FCSTD DOCUMENT  (FreeCAD 0.21R33668 +7 (Git))
Label: Headfixed Anaesthesia System
License: All rights reserved
LicenseURL: http://en.wikipedia.org/wiki/All_rights_reserved
objects: Sketcher::SketchObject×31, PartDesign::Pad×16, PartDesign::Pocket×10, Part::Feature×9, PartDesign::Body×5, Part::Box×2, Part::MultiCommon×2, Part::Mirroring×2, PartDesign::AdditiveLoft×2, PartDesign::LinearPattern×2, PartDesign::Chamfer×2, Mesh::Feature×1, Part::MultiFuse×1, Part::Cut×1, PartDesign::FeatureBase×1, Spreadsheet::Sheet×1, PartDesign::AdditivePipe×1, PartDesign::SubtractivePipe×1, PartDesign::Fillet×1, Part::Part2DObjectPython×1
note: 123 computed .brp shape members not serialized (recipe doc carries the construction recipe); baked Part::Feature solids carry a one-line shape summary decoded from their .brp

FEATURE [Mesh::Feature] MouseModel1_1_low_poly  label="MouseModel1.1_low_poly"
  Placement = pos=(-304.13,-78.83,-53.17) rot=(0,0,1;0rad)
FEATURE [Sketcher::SketchObject] Sketch  label="Mask profile"
  FullyConstrained = true
  MapMode = 5
  Placement = pos=(0,0,0) rot=(1,0,0;1.5708rad)
  Support = -> [XZ_Plane]
  expr: Constraints[19] = Spreadsheet.Hm
  expr: Constraints[20] = Spreadsheet.Wm
  expr: Constraints[21] = Spreadsheet.Rm
  expr: Constraints[27] = Spreadsheet.Ym
  sketch-geometry (12):
    g0: ArcOfCircle CenterX=-3.86 CenterY=1.095 CenterZ=0 NormalX=0 NormalY=0 NormalZ=1 AngleXU=0 Radius=2.26 StartAngle=1.5708 EndAngle=3.14159
    g1: LineSegment StartX=-3.86 StartY=3.355 StartZ=0 EndX=3.86 EndY=3.355 EndZ=0
    g2: ArcOfCircle CenterX=3.86 CenterY=1.095 CenterZ=0 NormalX=0 NormalY=0 NormalZ=1 AngleXU=0 Radius=2.26 StartAngle=1e-16 EndAngle=1.5708
    g3: LineSegment StartX=6.12 StartY=1.095 StartZ=0 EndX=6.12 EndY=-0.735 EndZ=0
    g4: ArcOfCircle CenterX=3.86 CenterY=-0.735 CenterZ=0 NormalX=0 NormalY=0 NormalZ=1 AngleXU=0 Radius=2.26 StartAngle=4.71239 EndAngle=6.28319
    g5: LineSegment StartX=3.86 StartY=-2.995 StartZ=0 EndX=-3.86 EndY=-2.995 EndZ=0
    g6: ArcOfCircle CenterX=-3.86 CenterY=-0.735 CenterZ=0 NormalX=0 NormalY=0 NormalZ=1 AngleXU=0 Radius=2.26 StartAngle=3.14159 EndAngle=4.71239
    g7: LineSegment StartX=-6.12 StartY=-0.735 StartZ=0 EndX=-6.12 EndY=1.095 EndZ=0
    g8: GeomPoint X=-6.12 Y=3.355 Z=0
    g9: GeomPoint X=6.12 Y=-2.995 Z=0
    g10: LineSegment StartX=-6.12 StartY=0.18 StartZ=0 EndX=6.12 EndY=0.18 EndZ=0
    g11: GeomPoint X=0 Y=0.18 Z=0
  constraints (28):
    c: Tangent(g0,g1) = 1.5708
    c: Tangent(g1,g2) = 1.5708
    c: Tangent(g2,g3) = 1.5708
    c: Tangent(g3,g4) = 1.5708
    c: Tangent(g4,g5) = 1.5708
    c: Tangent(g5,g6) = 1.5708
    c: Tangent(g6,g7) = 1.5708
    c: Tangent(g7,g0) = 1.5708
    c: Horizontal(g1)
    c: Horizontal(g5)
    c: Vertical(g3)
    c: Vertical(g7)
    c: Equal(g0,g2)
    c: Equal(g2,g4)
    c: PointOnObject(g8,g1)
    c: PointOnObject(g8,g7)
    c: PointOnObject(g9,g3)
    c: PointOnObject(g9,g5)
    c: Symmetric(g6,g4,g-2)
    c: DistanceY(g5,g0) = 6.35
    c: DistanceX(g0,g2) = 12.24
    c: Radius(g0) = 2.26
    c: PointOnObject(g10,g7)
    c: PointOnObject(g10,g3)
    c: Symmetric(g0,g5,g10)
    c: PointOnObject(g11,g10)
    c: PointOnObject(g11,g-2)
    c: DistanceY(g11) = 0.18
FEATURE [PartDesign::Pad] Pad
  Direction = (0,-1,-2e-16)
  Length = 1.5
  Length2 = 10
  Placement = pos=(0,0,0) rot=(1,0,0;1.5708rad)
  Profile = -> Sketch
  ReferenceAxis = -> Sketch [N_Axis]
  Type = 4
  expr: Length = Spreadsheet.YEm
FEATURE [PartDesign::Body] Body
  Group = -> [Sketch,Pad]
  Origin = -> Origin
  Tip = -> Pad
FEATURE [Part::Feature] MouseModel1_1_low_poly001_solid  label="MouseModel1_1_low_poly001 (Solid)"
  shape: large baked B-rep (84 MB .brp); summary skipped
FEATURE [Part::Feature] MouseModel1_1_low_poly001_solid001  label="MouseModel1_1_low_poly001 (Solid)001"
  shape: large baked B-rep (84 MB .brp); summary skipped
FEATURE [Part::Box] Box  label="Cube"
  AttacherType = Attacher::AttachEngine3D
  Height = 30
  Length = 40
  Placement = pos=(-20,-2,-12) rot=(0,0,1;0rad)
  Width = 30
FEATURE [Part::MultiCommon] Common
  Shapes = -> [MouseModel1_1_low_poly001_solid001,Box]
FEATURE [Part::Feature] Common001
  shape: bbox 33.9 x 28.08 x 25.21 mm, 16069 faces (baked)
FEATURE [Part::Box] Box001  label="Cube001"
  AttacherType = Attacher::AttachEngine3D
  Height = 20
  Length = 15
  Placement = pos=(-15,-1,-3.25) rot=(0,0,1;0rad)
  Width = 12
FEATURE [Part::MultiCommon] Common002
  Shapes = -> [Common001,Box001]
FEATURE [Part::Feature] Common002001
  shape: bbox 8.155 x 11.08 x 13.57 mm, 3527 faces (baked)
FEATURE [Part::Mirroring] Part__Mirroring  label="Common002001 (Mirror #1)"
  Base = (0,0,0)
  Normal = (1,0,0)
  Source = -> Common002001
FEATURE [Part::MultiFuse] Fusion
  Shapes = -> [Common002,Part__Mirroring]
FEATURE [Part::Cut] Cut
  Base = -> Body
  Tool = -> Fusion
FEATURE [PartDesign::FeatureBase] BaseFeature
  BaseFeature = -> Cut
FEATURE [Sketcher::SketchObject] Sketch002
  FullyConstrained = true
  MapMode = 5
  Placement = pos=(0,0,0) rot=(1,0,0;1.5708rad)
  Support = -> [XZ_Plane001]
  expr: Constraints[19] = Spreadsheet.Hm
  expr: Constraints[41] = Spreadsheet.Tm
  expr: Constraints[42] = Spreadsheet.Wm
  expr: Constraints[47] = Spreadsheet.Ym
  expr: Constraints[49] = Spreadsheet.Rm
  sketch-geometry (22):
    g0: ArcOfCircle CenterX=-3.86 CenterY=1.095 CenterZ=0 NormalX=0 NormalY=0 NormalZ=1 AngleXU=0 Radius=2.26 StartAngle=1.5708 EndAngle=3.14159
    g1: LineSegment StartX=-3.86 StartY=3.355 StartZ=0 EndX=3.86 EndY=3.355 EndZ=0
    g2: ArcOfCircle CenterX=3.86 CenterY=1.095 CenterZ=0 NormalX=0 NormalY=0 NormalZ=1 AngleXU=0 Radius=2.26 StartAngle=1e-16 EndAngle=1.5708
    g3: LineSegment StartX=6.12 StartY=1.095 StartZ=0 EndX=6.12 EndY=-0.735 EndZ=0
    g4: ArcOfCircle CenterX=3.86 CenterY=-0.735 CenterZ=0 NormalX=0 NormalY=0 NormalZ=1 AngleXU=0 Radius=2.26 StartAngle=4.71239 EndAngle=6.28319
    g5: LineSegment StartX=3.86 StartY=-2.995 StartZ=0 EndX=-3.86 EndY=-2.995 EndZ=0
    g6: ArcOfCircle CenterX=-3.86 CenterY=-0.735 CenterZ=0 NormalX=0 NormalY=0 NormalZ=1 AngleXU=0 Radius=2.26 StartAngle=3.14159 EndAngle=4.71239
    g7: LineSegment StartX=-6.12 StartY=-0.735 StartZ=0 EndX=-6.12 EndY=1.095 EndZ=0
    g8: GeomPoint X=-6.12 Y=3.355 Z=0
    g9: GeomPoint X=6.12 Y=-2.995 Z=0
    g10: ArcOfCircle CenterX=-3.86 CenterY=1.095 CenterZ=0 NormalX=0 NormalY=0 NormalZ=1 AngleXU=0 Radius=1.635 StartAngle=1.5708 EndAngle=3.14159
    g11: LineSegment StartX=-3.86 StartY=2.73 StartZ=0 EndX=3.86 EndY=2.73 EndZ=0
    g12: ArcOfCircle CenterX=3.86 CenterY=1.095 CenterZ=0 NormalX=0 NormalY=0 NormalZ=1 AngleXU=0 Radius=1.635 StartAngle=1e-16 EndAngle=1.5708
    g13: LineSegment StartX=5.495 StartY=1.095 StartZ=0 EndX=5.495 EndY=-0.735 EndZ=0
    g14: ArcOfCircle CenterX=3.86 CenterY=-0.735 CenterZ=0 NormalX=0 NormalY=0 NormalZ=1 AngleXU=0 Radius=1.635 StartAngle=4.71239 EndAngle=6.28319
    g15: LineSegment StartX=3.86 StartY=-2.37 StartZ=0 EndX=-3.86 EndY=-2.37 EndZ=0
    g16: ArcOfCircle CenterX=-3.86 CenterY=-0.735 CenterZ=0 NormalX=0 NormalY=0 NormalZ=1 AngleXU=0 Radius=1.635 StartAngle=3.14159 EndAngle=4.71239
    g17: LineSegment StartX=-5.495 StartY=-0.735 StartZ=0 EndX=-5.495 EndY=1.095 EndZ=0
    g18: GeomPoint X=-5.495 Y=2.73 Z=0
    g19: GeomPoint X=5.495 Y=-2.37 Z=0
    g20: LineSegment StartX=-6.12 StartY=0.18 StartZ=0 EndX=6.12 EndY=0.18 EndZ=0
    g21: GeomPoint X=0 Y=0.18 Z=0
  constraints (50):
    c: Tangent(g0,g1) = 1.5708
    c: Tangent(g1,g2) = 1.5708
    c: Tangent(g2,g3) = 1.5708
    c: Tangent(g3,g4) = 1.5708
    c: Tangent(g4,g5) = 1.5708
    c: Tangent(g5,g6) = 1.5708
    c: Tangent(g6,g7) = 1.5708
    c: Tangent(g7,g0) = 1.5708
    c: Horizontal(g1)
    c: Horizontal(g5)
    c: Vertical(g3)
    c: Vertical(g7)
    c: Equal(g0,g2)
    c: Equal(g2,g4)
    c: PointOnObject(g8,g1)
    c: PointOnObject(g8,g7)
    c: PointOnObject(g9,g3)
    c: PointOnObject(g9,g5)
    c: Symmetric(g6,g4,g-2)
    c: DistanceY(g5,g0) = 6.35
    c: Tangent(g10,g11) = 1.5708
    c: Tangent(g11,g12) = 1.5708
    c: Tangent(g12,g13) = 1.5708
    c: Tangent(g13,g14) = 1.5708
    c: Tangent(g14,g15) = 1.5708
    c: Tangent(g15,g16) = 1.5708
    c: Tangent(g16,g17) = 1.5708
    c: Tangent(g17,g10) = 1.5708
    c: Horizontal(g11)
    c: Horizontal(g15)
    c: Vertical(g13)
    c: Vertical(g17)
    c: Equal(g10,g12)
    c: Equal(g12,g14)
    c: Equal(g14,g16)
    c: PointOnObject(g18,g11)
    c: PointOnObject(g18,g17)
    c: PointOnObject(g19,g13)
    c: PointOnObject(g19,g15)
    c: Coincident(g0,g10)
    c: Coincident(g4,g14)
    c: DistanceX(g0,g10) = 0.625
    c: DistanceX(g0,g2) = 12.24
    c: PointOnObject(g20,g7)
    c: PointOnObject(g20,g3)
    c: PointOnObject(g21,g20)
    c: PointOnObject(g21,g-2)
    c: DistanceY(g21) = 0.18
    c: Symmetric(g0,g5,g20)
    c: Radius(g0) = 2.26
FEATURE [PartDesign::Pocket] Pocket
  BaseFeature = -> BaseFeature
  Direction = (0,1,2e-16)
  Length = 50
  Length2 = 0.875
  Profile = -> Sketch002
  ReferenceAxis = -> Sketch002 [N_Axis]
  Type = 4
  expr: Length2 = Spreadsheet.YEm - Spreadsheet.Tm
FEATURE [Spreadsheet::Sheet] Spreadsheet  label="params"
  cells = A4='Mask width; B4(Wm)==12.24 mm; A5='Mask height; B5(Hm)==6.35 mm; A6='Mask corner radius; B6(Rm)==2.26 mm; A7='Mask center y height; B7(Ym)==0.18 mm; A8='Mask thickness; B8(Tm)==0.625 mm; A9='Mask y extent; B9(YEm)==1.5 mm; A10='Tube outer diameter; B10(ODt)==0.125 "; A11='RightTubeZ; B11(Zrt)==Ym + Hm / 2 + ODt / 2 - Tm / 2 + 1 mm; A12='Tube inner diameter; B12(IDt)==3 " / 32; A13='Tube wall thickness; B13(WTt)==(ODt - IDt) / 2; A14='RightTubeY2; B14(Y2rt)==-YEm + Tm - WTt + ODt / 2 + ODt - WTt; A15='Mounting Hole X; B15(Xmh)==Xte + 12.75 mm - 25.5 mm - 2 mm; A16='Tube Y; B16(Yt)==YEm - Tm + WTt; A17='Mounting hole delta x; B17(DXmh)==0.25 "; A18='Mounting arm width; B18(Wma)==0.5 "; A19='Tube end X; B19(Xte)==30 mm
FEATURE [Sketcher::SketchObject] Sketch003  label="LeftTubeProfile"
  FullyConstrained = true
  MapMode = 5
  Placement = pos=(5.495,0,0) rot=(0.57735,-0.57735,-0.57735;2.0944rad)
  Support = -> [Pocket]
  expr: Constraints[1] = Spreadsheet.ODt
  expr: Constraints[4] = Spreadsheet.Yt
  sketch-geometry (2):
    g0: Circle CenterX=-0.315625 CenterY=0 CenterZ=0 NormalX=0 NormalY=0 NormalZ=1 AngleXU=0 Radius=1.5875
    g1: GeomPoint X=1.27188 Y=0 Z=0
  constraints (5):
    c: PointOnObject(g0,g-1)
    c: Diameter(g0) = 3.175
    c: PointOnObject(g1,g0)
    c: PointOnObject(g1,g-1)
    c: DistanceX(g1) = 1.27188
FEATURE [PartDesign::Pad] Pad001
  BaseFeature = -> Pocket
  Direction = (-1,0,0)
  Length = 24.5
  Length2 = 10
  Profile = -> Sketch003
  ReferenceAxis = -> Sketch003 [N_Axis]
  Reversed = true
  Type = 0
  expr: Length = Spreadsheet.Xte - 5.5 mm
FEATURE [Sketcher::SketchObject] Sketch004  label="RightTubeProfile"
  FullyConstrained = true
  MapMode = 5
  Placement = pos=(-5.495,0,0) rot=(0.57735,0.57735,0.57735;2.0944rad)
  Support = -> [Pad001]
  expr: Constraints[3] = -Spreadsheet.Yt
  expr: Constraints[4] = Spreadsheet.ODt
  sketch-geometry (2):
    g0: Circle CenterX=0.315625 CenterY=0 CenterZ=0 NormalX=0 NormalY=0 NormalZ=1 AngleXU=0 Radius=1.5875
    g1: GeomPoint X=-1.27188 Y=0 Z=0
  constraints (5):
    c: PointOnObject(g0,g-1)
    c: PointOnObject(g1,g0)
    c: PointOnObject(g1,g-1)
    c: DistanceX(g1) = -1.27188
    c: Diameter(g0) = 3.175
FEATURE [Sketcher::SketchObject] Sketch005  label="RightTubePath1"
  FullyConstrained = true
  MapMode = 5
  Placement = pos=(0,1.27188,0) rot=(1,0,0;1.5708rad)
  expr: .Placement.Base.y = Spreadsheet.Yt
  expr: Constraints[2] = -Spreadsheet.Wm / 2 + Spreadsheet.Tm
  expr: Constraints[3] = Spreadsheet.Tm
  expr: Constraints[6] = Spreadsheet.Zrt
  expr: Constraints[9] = Spreadsheet.Xte
  sketch-geometry (3):
    g0: LineSegment StartX=-5.495 StartY=0 StartZ=0 EndX=-6.12 EndY=4e-16 EndZ=0
    g1: ArcOfCircle CenterX=-6.12 CenterY=2.815 CenterZ=0 NormalX=0 NormalY=0 NormalZ=1 AngleXU=0 Radius=2.815 StartAngle=1.5708 EndAngle=4.71239
    g2: LineSegment StartX=-6.12 StartY=5.63 StartZ=0 EndX=30 EndY=5.63 EndZ=0
  constraints (10):
    c: PointOnObject(g0,g-1)
    c: PointOnObject(g0,g-1)
    c: DistanceX(g0) = -5.495
    c: DistanceX(g0,g0) = 0.625
    c: Tangent(g1,g0) = 1.5708
    c: DistanceX(g1,g1) = 0
    c: DistanceY(g1) = 5.63
    c: Coincident(g2,g1)
    c: Horizontal(g2)
    c: DistanceX(g2) = 30
FEATURE [PartDesign::AdditivePipe] AdditivePipe
  AuxilleryCurvelinear = true
  AuxillerySpineTangent = false
  BaseFeature = -> Pad001
  Binormal = (0,0,0)
  Mode = 0
  Profile = -> Sketch004
  Spine = -> Sketch005
  SpineTangent = false
  Transformation = 0
  Transition = 0
FEATURE [Sketcher::SketchObject] Sketch006  label="TubeJoiner"
  FullyConstrained = true
  MapMode = 5
  Placement = pos=(0,0.315625,0) rot=(1,0,0;1.5708rad)
  expr: .Placement.Base.y = -Spreadsheet.YEm + Spreadsheet.Tm - Spreadsheet.WTt + Spreadsheet.ODt / 2
  expr: Constraints[12] = Spreadsheet.Wm / 2 - Spreadsheet.Rm
  expr: Constraints[13] = Spreadsheet.Zrt
  expr: Constraints[28] = Spreadsheet.Xte - 7.5 mm - 0.9 mm
  expr: Constraints[8] = Spreadsheet.Ym + Spreadsheet.Hm / 2 - Spreadsheet.Rm
  expr: Constraints[9] = Spreadsheet.Rm
  sketch-geometry (9):
    g0: ArcOfCircle CenterX=3.86 CenterY=1.095 CenterZ=0 NormalX=0 NormalY=0 NormalZ=1 AngleXU=0 Radius=2.26 StartAngle=0 EndAngle=1.5708
    g1: LineSegment StartX=6.12 StartY=1.095 StartZ=0 EndX=6.12 EndY=0 EndZ=0
    g2: LineSegment StartX=6.12 StartY=0 StartZ=0 EndX=21.6 EndY=0 EndZ=0
    g3: LineSegment StartX=21.6 StartY=0 StartZ=0 EndX=21.6 EndY=5.63 EndZ=0
    g4: LineSegment StartX=21.6 StartY=5.63 StartZ=0 EndX=-6.12 EndY=5.63 EndZ=0
    g5: ArcOfCircle CenterX=-6.12 CenterY=2.815 CenterZ=0 NormalX=0 NormalY=0 NormalZ=1 AngleXU=0 Radius=2.815 StartAngle=1.5708 EndAngle=4.71239
    g6: ArcOfCircle CenterX=-3.86 CenterY=1.095 CenterZ=0 NormalX=0 NormalY=0 NormalZ=1 AngleXU=0 Radius=2.26 StartAngle=1.5708 EndAngle=3.14159
    g7: LineSegment StartX=-6.12 StartY=1.095 StartZ=0 EndX=-6.12 EndY=0 EndZ=0
    g8: LineSegment StartX=-3.86 StartY=3.355 StartZ=0 EndX=3.86 EndY=3.355 EndZ=0
  constraints (29):
    c: Coincident(g1,g0)
    c: Vertical(g1)
    c: Coincident(g1,g2)
    c: Horizontal(g2)
    c: Coincident(g2,g3)
    c: Vertical(g3)
    c: Coincident(g3,g4)
    c: Horizontal(g4)
    c: DistanceY(g0) = 1.095
    c: Radius(g0) = 2.26
    c: DistanceX(g0,g0) = 0
    c: DistanceY(g0,g0) = 0
    c: DistanceX(g0) = 3.86
    c: DistanceY(g4) = 5.63
    c: DistanceY(g2) = 0
    c: Coincident(g5,g4)
    c: PointOnObject(g5,g-1)
    c: Coincident(g7,g6)
    c: Coincident(g7,g5)
    c: Coincident(g8,g6)
    c: Coincident(g8,g0)
    c: Horizontal(g8)
    c: DistanceY(g6,g6) = 0
    c: DistanceX(g6,g6) = 0
    c: Vertical(g7)
    c: DistanceX(g5,g5) = 0
    c: DistanceX(g5,g4) = 0
    c: Symmetric(g6,g0,g-2)
    c: DistanceX(g3) = 21.6
FEATURE [PartDesign::Pad] Pad002
  BaseFeature = -> AdditivePipe
  Direction = (0,-1,2e-16)
  Length = 3.175
  Length2 = 10
  Midplane = true
  Profile = -> Sketch006
  ReferenceAxis = -> Sketch006 [N_Axis]
  Type = 0
  expr: Length = Spreadsheet.ODt
FEATURE [Sketcher::SketchObject] Sketch007  label="LeftTubeProfile001"
  FullyConstrained = true
  MapMode = 5
  Placement = pos=(5.495,0,0) rot=(0.57735,-0.57735,-0.57735;2.0944rad)
  Support = -> [Pocket]
  expr: Constraints[1] = Spreadsheet.ODt
  expr: Constraints[4] = Spreadsheet.YEm - Spreadsheet.Tm + Spreadsheet.WTt
  expr: Constraints[6] = Spreadsheet.IDt
  sketch-geometry (3):
    g0: Circle CenterX=-0.315625 CenterY=0 CenterZ=0 NormalX=0 NormalY=0 NormalZ=1 AngleXU=0 Radius=1.5875
    g1: GeomPoint X=1.27188 Y=0 Z=0
    g2: Circle CenterX=-0.315625 CenterY=0 CenterZ=0 NormalX=0 NormalY=0 NormalZ=1 AngleXU=0 Radius=1.19062
  constraints (7):
    c: PointOnObject(g0,g-1)
    c: Diameter(g0) = 3.175
    c: PointOnObject(g1,g0)
    c: PointOnObject(g1,g-1)
    c: DistanceX(g1) = 1.27188
    c: Coincident(g2,g0)
    c: Diameter(g2) = 2.38125
FEATURE [Sketcher::SketchObject] Sketch008  label="RightTubeProfile001"
  FullyConstrained = true
  MapMode = 5
  Placement = pos=(-5.495,0,0) rot=(0.57735,0.57735,0.57735;2.0944rad)
  Support = -> [Pad001]
  expr: Constraints[3] = -Spreadsheet.YEm + Spreadsheet.Tm - Spreadsheet.WTt
  expr: Constraints[4] = Spreadsheet.ODt
  expr: Constraints[6] = Spreadsheet.IDt
  sketch-geometry (3):
    g0: Circle CenterX=0.315625 CenterY=0 CenterZ=0 NormalX=0 NormalY=0 NormalZ=1 AngleXU=0 Radius=1.5875
    g1: GeomPoint X=-1.27188 Y=0 Z=0
    g2: Circle CenterX=0.315625 CenterY=0 CenterZ=0 NormalX=0 NormalY=0 NormalZ=1 AngleXU=0 Radius=1.19062
  constraints (7):
    c: PointOnObject(g0,g-1)
    c: PointOnObject(g1,g0)
    c: PointOnObject(g1,g-1)
    c: DistanceX(g1) = -1.27188
    c: Diameter(g0) = 3.175
    c: Coincident(g2,g0)
    c: Diameter(g2) = 2.38125
FEATURE [PartDesign::Pocket] Pocket001
  BaseFeature = -> Pad002
  Direction = (1,0,0)
  Length = 5
  Length2 = 5
  Profile = -> Sketch007
  ReferenceAxis = -> Sketch007 [N_Axis]
  Type = 1
FEATURE [PartDesign::SubtractivePipe] SubtractivePipe
  AuxilleryCurvelinear = true
  AuxillerySpineTangent = false
  BaseFeature = -> Pocket001
  Binormal = (0,0,0)
  Mode = 0
  Profile = -> Sketch008
  Spine = -> Sketch005
  SpineTangent = false
  Transformation = 0
  Transition = 0
FEATURE [Part::Feature] Part__Feature  label="5372K511_Plastic Barbed Tube Fitting for Air and Water"
  Placement = pos=(30.46,-4.33,0) rot=(0,0,1;0rad)
  shape: bbox 22.86 x 4.562 x 4.562 mm, 34 faces (baked)
FEATURE [Sketcher::SketchObject] Sketch009  label="BarbProfile1"
  FullyConstrained = true
  MapMode = 5
  Placement = pos=(30,0,0) rot=(0.57735,0.57735,0.57735;2.0944rad)
  Support = -> [SubtractivePipe]
  expr: Constraints[1] = Spreadsheet.IDt
  expr: Constraints[2] = Spreadsheet.ODt
  expr: Constraints[3] = Spreadsheet.Zrt
  expr: Constraints[4] = -Spreadsheet.YEm + Spreadsheet.Tm - Spreadsheet.WTt + Spreadsheet.ODt / 2
  sketch-geometry (2):
    g0: Circle CenterX=0.315625 CenterY=5.63 CenterZ=0 NormalX=0 NormalY=0 NormalZ=1 AngleXU=0 Radius=1.5875
    g1: Circle CenterX=0.315625 CenterY=5.63 CenterZ=0 NormalX=0 NormalY=0 NormalZ=1 AngleXU=0 Radius=1.19062
  constraints (5):
    c: Coincident(g1,g0)
    c: Diameter(g1) = 2.38125
    c: Diameter(g0) = 3.175
    c: DistanceY(g0) = 5.63
    c: DistanceX(g0) = 0.315625
FEATURE [Sketcher::SketchObject] Sketch010  label="BarbProfile2"
  FullyConstrained = true
  MapMode = 5
  Placement = pos=(28.1,0,0) rot=(0.57735,0.57735,0.57735;2.0944rad)
  expr: .Placement.Base.x = Spreadsheet.Xte - 1.9 mm
  expr: Constraints[1] = Spreadsheet.IDt
  expr: Constraints[2] = Spreadsheet.ODt + 0.31 mm
  expr: Constraints[3] = Spreadsheet.Zrt
  expr: Constraints[4] = -Spreadsheet.YEm + Spreadsheet.Tm - Spreadsheet.WTt + Spreadsheet.ODt / 2
  sketch-geometry (2):
    g0: Circle CenterX=0.315625 CenterY=5.63 CenterZ=0 NormalX=0 NormalY=0 NormalZ=1 AngleXU=0 Radius=1.7425
    g1: Circle CenterX=0.315625 CenterY=5.63 CenterZ=0 NormalX=0 NormalY=0 NormalZ=1 AngleXU=0 Radius=1.19062
  constraints (5):
    c: Coincident(g1,g0)
    c: Diameter(g1) = 2.38125
    c: Diameter(g0) = 3.485
    c: DistanceY(g0) = 5.63
    c: DistanceX(g0) = 0.315625
FEATURE [PartDesign::AdditiveLoft] AdditiveLoft
  BaseFeature = -> SubtractivePipe
  Closed = false
  Profile = -> Sketch009
  Ruled = false
  Sections = -> [Sketch010]
FEATURE [PartDesign::LinearPattern] LinearPattern
  BaseFeature = -> AdditiveLoft
  Direction = -> Sketch009 [N_Axis]
  Length = 3.8
  Occurrences = 3
  Originals = -> [AdditiveLoft]
  Reversed = true
  expr: Length = 1.9 mm * 2
FEATURE [Sketcher::SketchObject] Sketch011  label="BarbProfile003"
  FullyConstrained = true
  MapMode = 5
  Placement = pos=(30,0,0) rot=(0.57735,0.57735,0.57735;2.0944rad)
  Support = -> [SubtractivePipe]
  expr: Constraints[1] = Spreadsheet.IDt
  expr: Constraints[2] = Spreadsheet.ODt
  expr: Constraints[3] = -Spreadsheet.YEm + Spreadsheet.Tm - Spreadsheet.WTt + Spreadsheet.ODt / 2
  sketch-geometry (2):
    g0: Circle CenterX=0.315625 CenterY=0 CenterZ=0 NormalX=0 NormalY=0 NormalZ=1 AngleXU=0 Radius=1.5875
    g1: Circle CenterX=0.315625 CenterY=0 CenterZ=0 NormalX=0 NormalY=0 NormalZ=1 AngleXU=0 Radius=1.19062
  constraints (5):
    c: Coincident(g1,g0)
    c: Diameter(g1) = 2.38125
    c: Diameter(g0) = 3.175
    c: DistanceX(g0) = 0.315625
    c: DistanceY(g0) = 0
FEATURE [Sketcher::SketchObject] Sketch012  label="BarbProfile004"
  FullyConstrained = true
  MapMode = 5
  Placement = pos=(28.1,0,0) rot=(0.57735,0.57735,0.57735;2.0944rad)
  expr: .Placement.Base.x = Spreadsheet.Xte - 1.9 mm
  expr: Constraints[1] = Spreadsheet.IDt
  expr: Constraints[2] = Spreadsheet.ODt + 0.31 mm
  expr: Constraints[4] = -Spreadsheet.YEm + Spreadsheet.Tm - Spreadsheet.WTt + Spreadsheet.ODt / 2
  sketch-geometry (2):
    g0: Circle CenterX=0.315625 CenterY=0 CenterZ=0 NormalX=0 NormalY=0 NormalZ=1 AngleXU=0 Radius=1.7425
    g1: Circle CenterX=0.315625 CenterY=0 CenterZ=0 NormalX=0 NormalY=0 NormalZ=1 AngleXU=0 Radius=1.19062
  constraints (5):
    c: Coincident(g1,g0)
    c: Diameter(g1) = 2.38125
    c: Diameter(g0) = 3.485
    c: DistanceY(g0) = 0
    c: DistanceX(g0) = 0.315625
FEATURE [PartDesign::AdditiveLoft] AdditiveLoft001
  BaseFeature = -> LinearPattern
  Closed = false
  Profile = -> Sketch011
  Ruled = false
  Sections = -> [Sketch012]
FEATURE [PartDesign::LinearPattern] LinearPattern001
  BaseFeature = -> AdditiveLoft001
  Direction = -> Sketch011 [N_Axis]
  Length = 3.8
  Occurrences = 3
  Originals = -> [AdditiveLoft001]
  Reversed = true
  expr: Length = 1.9 mm * 2
FEATURE [Sketcher::SketchObject] Sketch013  label="Mounting holes"
  FullyConstrained = true
  MapMode = 5
  Placement = pos=(0,-1.27187,3e-16) rot=(1,0,0;1.5708rad)
  Support = -> [LinearPattern001]
  expr: Constraints[0] = 0.12 "
  expr: Constraints[15] = Spreadsheet.Xmh
  expr: Constraints[16] = Spreadsheet.DXmh
  expr: Constraints[1] = Spreadsheet.Zrt / 2
  expr: Constraints[5] = 0.219 "
  sketch-geometry (8):
    g0: Circle CenterX=12.075 CenterY=2.815 CenterZ=0 NormalX=0 NormalY=0 NormalZ=1 AngleXU=0 Radius=1.524
    g1: Circle CenterX=18.425 CenterY=2.815 CenterZ=0 NormalX=0 NormalY=0 NormalZ=1 AngleXU=0 Radius=1.524
    g2: Circle CenterX=12.075 CenterY=2.815 CenterZ=0 NormalX=0 NormalY=0 NormalZ=1 AngleXU=0 Radius=2.84073
    g3: Circle CenterX=18.425 CenterY=2.815 CenterZ=0 NormalX=0 NormalY=0 NormalZ=1 AngleXU=0 Radius=2.84073
    g4: GeomPoint X=15.5843 Y=2.815 Z=0
    g5: GeomPoint X=14.9157 Y=2.815 Z=0
    g6: LineSegment StartX=12.075 StartY=2.815 StartZ=0 EndX=18.425 EndY=2.815 EndZ=0
    g7: GeomPoint X=15.25 Y=2.815 Z=0
  constraints (17):
    c: Diameter(g0) = 3.048
    c: DistanceY(g0) = 2.815
    c: Equal(g1,g0)
    c: DistanceY(g0,g1) = 0
    c: Coincident(g2,g0)
    c: Diameter(g2) = 5.68146
    c: Coincident(g3,g1)
    c: Equal(g3,g2)
    c: PointOnObject(g4,g3)
    c: PointOnObject(g5,g2)
    c: Coincident(g6,g0)
    c: Coincident(g6,g1)
    c: PointOnObject(g4,g6)
    c: PointOnObject(g5,g6)
    c: Symmetric(g0,g1,g7)
    c: DistanceX(g7) = 15.25
    c: DistanceX(g0,g1) = 6.35
FEATURE [PartDesign::Pocket] Pocket002
  BaseFeature = -> LinearPattern001
  Direction = (0,1,-2e-16)
  Length = 5
  Length2 = 5
  Profile = -> Sketch013
  ReferenceAxis = -> Sketch013 [N_Axis]
  Type = 1
FEATURE [PartDesign::Body] Body001  label="Mask"
  BaseFeature = -> Cut
  Group = -> [BaseFeature,Sketch002,Pocket,Sketch003,Pad001,Sketch004,Sketch005,AdditivePipe,Sketch006,Pad002,Sketch007,Sketch008,Pocket001,SubtractivePipe,Sketch009,Sketch010,AdditiveLoft,LinearPattern,Sketch011,Sketch012,AdditiveLoft001,LinearPattern001,Sketch013,Pocket002]
  Origin = -> Origin001
  Tip = -> Pocket002
FEATURE [Sketcher::SketchObject] Sketch014  label="ConnectorProfile"
  FullyConstrained = true
  MapMode = 5
  Placement = pos=(15.25,0,0) rot=(0.57735,0.57735,0.57735;2.0944rad)
  expr: .Placement.Base.x = Spreadsheet.Xmh
  expr: Constraints[23] = -Spreadsheet.Yt
  expr: Constraints[24] = Spreadsheet.ODt
  expr: Constraints[25] = 1.1 * Spreadsheet.ODt
  expr: Constraints[27] = Spreadsheet.Zrt
  expr: Constraints[28] = Spreadsheet.ODt * 2
  sketch-geometry (12):
    g0: ArcOfCircle CenterX=0.315625 CenterY=0 CenterZ=0 NormalX=0 NormalY=0 NormalZ=1 AngleXU=0 Radius=1.74625 StartAngle=3.14159 EndAngle=6.28319
    g1: ArcOfCircle CenterX=0.315625 CenterY=0 CenterZ=0 NormalX=0 NormalY=0 NormalZ=1 AngleXU=0 Radius=3.175 StartAngle=4.71239 EndAngle=6.28319
    g2: ArcOfCircle CenterX=-1.43063 CenterY=4.20125 CenterZ=0 NormalX=0 NormalY=0 NormalZ=1 AngleXU=0 Radius=1.42875 StartAngle=1.5708 EndAngle=3.14159
    g3: ArcOfCircle CenterX=2.06188 CenterY=4.20125 CenterZ=0 NormalX=0 NormalY=0 NormalZ=1 AngleXU=0 Radius=1.42875 StartAngle=0 EndAngle=1.5708
    g4: LineSegment StartX=-2.85937 StartY=4.20125 StartZ=0 EndX=-2.85937 EndY=-3.175 EndZ=0
    g5: LineSegment StartX=-1.43063 StartY=5.63 StartZ=0 EndX=-1.43063 EndY=0 EndZ=0
    g6: LineSegment StartX=2.06188 StartY=5.63 StartZ=0 EndX=2.06188 EndY=0 EndZ=0
    g7: LineSegment StartX=3.49062 StartY=4.20125 StartZ=0 EndX=3.49062 EndY=-9e-16 EndZ=0
    g8: Circle CenterX=0.315625 CenterY=0 CenterZ=0 NormalX=0 NormalY=0 NormalZ=1 AngleXU=0 Radius=1.5875
    g9: GeomPoint X=-1.27188 Y=0 Z=0
    g10: LineSegment StartX=-2.85937 StartY=-3.175 StartZ=0 EndX=0.315625 EndY=-3.175 EndZ=0
    g11: LineSegment StartX=0.315625 StartY=0 StartZ=0 EndX=0.315625 EndY=-3.175 EndZ=0
  constraints (35):
    c: PointOnObject(g0,g-1)
    c: PointOnObject(g0,g-1)
    c: PointOnObject(g0,g-1)
    c: Coincident(g1,g0)
    c: PointOnObject(g1,g-1)
    c: Coincident(g4,g2)
    c: Vertical(g4)
    c: Coincident(g5,g2)
    c: Coincident(g5,g0)
    c: Coincident(g6,g3)
    c: Coincident(g6,g0)
    c: Coincident(g7,g3)
    c: Coincident(g7,g1)
    c: Vertical(g7)
    c: Vertical(g5)
    c: Vertical(g6)
    c: Equal(g3,g2)
    c: PointOnObject(g2,g5)
    c: DistanceY(g2,g2) = 0
    c: DistanceY(g3,g3) = 0
    c: Coincident(g8,g0)
    c: PointOnObject(g9,g8)
    c: PointOnObject(g9,g-1)
    c: DistanceX(g9) = -1.27188
    c: Diameter(g8) = 3.175
    c: Diameter(g0) = 3.4925
    c: DistanceY(g3,g2) = 0
    c: DistanceY(g2) = 5.63
    c: Diameter(g1) = 6.35
    c: Coincident(g10,g4)
    c: Coincident(g10,g1)
    c: Horizontal(g10)
    c: Coincident(g11,g0)
    c: Coincident(g1,g11)
    c: Symmetric(g2,g3,g11)
FEATURE [PartDesign::Pad] Pad003
  Direction = (1,0,0)
  Length = 12.7
  Length2 = 10
  Midplane = true
  Placement = pos=(15.25,0,0) rot=(0.57735,0.57735,0.57735;2.0944rad)
  Profile = -> Sketch014
  ReferenceAxis = -> Sketch014 [N_Axis]
  Type = 0
  expr: Length = Spreadsheet.Wma
FEATURE [Sketcher::SketchObject] Sketch015  label="Mounting holes001"
  FullyConstrained = true
  MapMode = 5
  Placement = pos=(0,-1.27187,3e-16) rot=(1,0,0;1.5708rad)
  Support = -> [LinearPattern001]
  expr: Constraints[0] = 0.12 "
  expr: Constraints[15] = Spreadsheet.Xmh
  expr: Constraints[16] = Spreadsheet.DXmh
  expr: Constraints[1] = Spreadsheet.Zrt / 2
  expr: Constraints[5] = 0.219 "
  sketch-geometry (8):
    g0: Circle CenterX=12.075 CenterY=2.815 CenterZ=0 NormalX=0 NormalY=0 NormalZ=1 AngleXU=0 Radius=1.524
    g1: Circle CenterX=18.425 CenterY=2.815 CenterZ=0 NormalX=0 NormalY=0 NormalZ=1 AngleXU=0 Radius=1.524
    g2: Circle CenterX=12.075 CenterY=2.815 CenterZ=0 NormalX=0 NormalY=0 NormalZ=1 AngleXU=0 Radius=2.84073
    g3: Circle CenterX=18.425 CenterY=2.815 CenterZ=0 NormalX=0 NormalY=0 NormalZ=1 AngleXU=0 Radius=2.84073
    g4: GeomPoint X=15.5843 Y=2.815 Z=0
    g5: GeomPoint X=14.9157 Y=2.815 Z=0
    g6: LineSegment StartX=12.075 StartY=2.815 StartZ=0 EndX=18.425 EndY=2.815 EndZ=0
    g7: GeomPoint X=15.25 Y=2.815 Z=0
  constraints (17):
    c: Diameter(g0) = 3.048
    c: DistanceY(g0) = 2.815
    c: Equal(g1,g0)
    c: DistanceY(g0,g1) = 0
    c: Coincident(g2,g0)
    c: Diameter(g2) = 5.68146
    c: Coincident(g3,g1)
    c: Equal(g3,g2)
    c: PointOnObject(g4,g3)
    c: PointOnObject(g5,g2)
    c: Coincident(g6,g0)
    c: Coincident(g6,g1)
    c: PointOnObject(g4,g6)
    c: PointOnObject(g5,g6)
    c: Symmetric(g0,g1,g7)
    c: DistanceX(g7) = 15.25
    c: DistanceX(g0,g1) = 6.35
FEATURE [PartDesign::Pocket] Pocket003
  BaseFeature = -> Pad003
  Direction = (0,1,-2e-16)
  Length = 5
  Length2 = 5
  Midplane = true
  Placement = pos=(15.25,0,0) rot=(0.57735,0.57735,0.57735;2.0944rad)
  Profile = -> Sketch015
  ReferenceAxis = -> Sketch015 [N_Axis]
  Type = 1
FEATURE [Sketcher::SketchObject] Sketch016  label="Mounting arm profile"
  FullyConstrained = true
  MapMode = 5
  Placement = pos=(15.25,-2.85937,2e-16) rot=(0.57735,0.57735,-0.57735;2.0944rad)
  Support = -> [Pocket003]
  expr: Constraints[13] = Spreadsheet.DXmh
  expr: Constraints[14] = -Spreadsheet.Zrt / 2
  expr: Constraints[15] = 0.219 "
  expr: Constraints[16] = Spreadsheet.Wma
  expr: Constraints[18] = Spreadsheet.ODt
  sketch-geometry (8):
    g0: LineSegment StartX=3.175 StartY=6.35 StartZ=0 EndX=0 EndY=6.35 EndZ=0
    g1: LineSegment StartX=0 StartY=6.35 StartZ=0 EndX=0 EndY=-6.35 EndZ=0
    g2: LineSegment StartX=0 StartY=-6.35 StartZ=0 EndX=3.175 EndY=-6.35 EndZ=0
    g3: LineSegment StartX=3.175 StartY=-6.35 StartZ=0 EndX=3.175 EndY=6.35 EndZ=0
    g4: Circle CenterX=-2.815 CenterY=3.175 CenterZ=0 NormalX=0 NormalY=0 NormalZ=1 AngleXU=0 Radius=2.7813
    g5: Circle CenterX=-2.815 CenterY=-3.175 CenterZ=0 NormalX=0 NormalY=0 NormalZ=1 AngleXU=0 Radius=2.7813
    g6: GeomPoint X=-2.815 Y=0.3937 Z=0
    g7: GeomPoint X=-2.815 Y=-0.3937 Z=0
  constraints (20):
    c: Coincident(g0,g1)
    c: Coincident(g1,g2)
    c: Coincident(g2,g3)
    c: Coincident(g3,g0)
    c: Horizontal(g0)
    c: Horizontal(g2)
    c: Vertical(g1)
    c: Equal(g5,g4)
    c: Symmetric(g5,g4,g-1)
    c: PointOnObject(g6,g4)
    c: PointOnObject(g7,g5)
    c: DistanceX(g6,g4) = 0
    c: DistanceX(g7,g5) = 0
    c: DistanceY(g5,g4) = 6.35
    c: DistanceX(g4) = -2.815
    c: Diameter(g4) = 5.5626
    c: DistanceY(g3,g3) = 12.7
    c: Symmetric(g0,g2,g-1)
    c: DistanceX(g0) = 3.175
    c: DistanceX(g0,g0) = 3.175
FEATURE [Sketcher::SketchObject] Sketch020  label="Mounting platform"
  FullyConstrained = false
  MapMode = 5
  Support = -> [XY_Plane003]
  sketch-geometry (4):
    g0: LineSegment StartX=-25.4 StartY=3.175 StartZ=0 EndX=0 EndY=3.175 EndZ=0
    g1: LineSegment StartX=0 StartY=3.175 StartZ=0 EndX=0 EndY=0 EndZ=0
    g2: LineSegment StartX=0 StartY=0 StartZ=0 EndX=-25.4 EndY=0 EndZ=0
    g3: LineSegment StartX=-25.4 StartY=0 StartZ=0 EndX=-25.4 EndY=3.175 EndZ=0
  constraints (11):
    c: Coincident(g0,g1)
    c: Coincident(g1,g2)
    c: Coincident(g2,g3)
    c: Coincident(g3,g0)
    c: Horizontal(g0)
    c: Horizontal(g2)
    c: Vertical(g1)
    c: Vertical(g3)
    c: DistanceX(g2,g2) = 25.4
    c: DistanceY(g1,g1) = 3.175
    c: Coincident(g-1,g1)
FEATURE [PartDesign::Pad] Pad005
  AllowMultiFace = false
  Direction = (1,1,1)
  Length = 25.4
  Length2 = 99.9998
  Profile = -> Sketch020
  Type = 0
FEATURE [Sketcher::SketchObject] Sketch001  label="Spout support platform"
  FullyConstrained = false
  MapMode = 5
  Placement = pos=(0,3.175,0) rot=(0,0.707107,0.707107;3.14159rad)
  Support = -> [Pad005]
  expr: Constraints[11] = 1.5 in - 0.375 in
  expr: Constraints[8] = (1 in - 0.4 in) / 2
  sketch-geometry (4):
    g0: LineSegment StartX=-28.575 StartY=17.78 StartZ=0 EndX=0 EndY=17.78 EndZ=0
    g1: LineSegment StartX=0 StartY=17.78 StartZ=0 EndX=0 EndY=7.62 EndZ=0
    g2: LineSegment StartX=0 StartY=7.62 StartZ=0 EndX=-28.575 EndY=7.62 EndZ=0
    g3: LineSegment StartX=-28.575 StartY=7.62 StartZ=0 EndX=-28.575 EndY=17.78 EndZ=0
  constraints (12):
    c: Coincident(g0,g1)
    c: Coincident(g1,g2)
    c: Coincident(g2,g3)
    c: Coincident(g3,g0)
    c: Horizontal(g0)
    c: Horizontal(g2)
    c: Vertical(g1)
    c: Vertical(g3)
    c: DistanceY(g-1,g1) = 7.62
    c: DistanceY(g1,g1) = 10.16
    c: DistanceX(g1,g-1) = 0
    c: DistanceX(g2,g2) = 28.575
FEATURE [PartDesign::Pad] Pad006
  AllowMultiFace = false
  BaseFeature = -> Pad005
  Direction = (1,1,1)
  Length = 1.81
  Length2 = 4.445
  Profile = -> Sketch001
  Type = 4
  expr: Length = 1.81 mm
FEATURE [Sketcher::SketchObject] Sketch021  label="Spout groove"
  FullyConstrained = false
  MapMode = 5
  Placement = pos=(28.575,0,0) rot=(0.57735,0.57735,0.57735;2.0944rad)
  Support = -> [Pad006]
  expr: Constraints[3] = 1.81 mm / 2
  expr: Constraints[7] = 0.125 " + 1.81 mm / 2
  sketch-geometry (4):
    g0: LineSegment StartX=9.15014 StartY=19.05 StartZ=0 EndX=2.80014 EndY=12.7 EndZ=0
    g1: LineSegment StartX=2.80014 StartY=12.7 StartZ=0 EndX=9.15014 EndY=6.35 EndZ=0
    g2: LineSegment StartX=9.15014 StartY=6.35 StartZ=0 EndX=9.15014 EndY=19.05 EndZ=0
    g3: Circle CenterX=4.08 CenterY=12.7 CenterZ=0 NormalX=0 NormalY=0 NormalZ=1 AngleXU=0 Radius=0.905
  constraints (12):
    c: Coincident(g0,g2)
    c: Coincident(g0,g1)
    c: Coincident(g1,g2)
    c: Radius(g3) = 0.905
    c: Tangent(g1,g3)
    c: Tangent(g3,g0)
    c: DistanceX(g1,g0) = 0
    c: DistanceX(g-1,g3) = 4.08
    c: DistanceY(g-1,g0) = 12.7
    c: Equal(g0,g1)
    c: Angle(g1,g0) = 1.5708
    c: DistanceX(g0,g1) = 6.35
FEATURE [PartDesign::Pocket] Pocket004
  AllowMultiFace = false
  BaseFeature = -> Pad006
  Direction = (1,1,1)
  Length = 9.525
  Length2 = 99.9998
  Profile = -> Sketch021
  Type = 0
  expr: Length = 3 in / 8
FEATURE [Sketcher::SketchObject] Sketch022  label="Tube groove"
  FullyConstrained = false
  MapMode = 5
  Placement = pos=(19.05,0,0) rot=(0.57735,0.57735,0.57735;2.0944rad)
  Support = -> [Pocket004]
  expr: Constraints[12] = 1.81 mm / 2
  expr: Constraints[2] = 0.16 " / 2
  expr: Constraints[4] = 0.125 " + 1.81 mm / 2
  sketch-geometry (4):
    g0: ArcOfCircle CenterX=4.08 CenterY=12.7 CenterZ=0 NormalX=0 NormalY=0 NormalZ=1 AngleXU=0 Radius=2.032 StartAngle=1.5708 EndAngle=4.71239
    g1: LineSegment StartX=4.08 StartY=14.732 StartZ=0 EndX=4.985 EndY=14.732 EndZ=0
    g2: LineSegment StartX=4.985 StartY=14.732 StartZ=0 EndX=4.985 EndY=10.668 EndZ=0
    g3: LineSegment StartX=4.985 StartY=10.668 StartZ=0 EndX=4.08 EndY=10.668 EndZ=0
  constraints (13):
    c: DistanceX(g0,g0) = 0
    c: DistanceX(g0,g0) = 0
    c: Radius(g0) = 2.032
    c: DistanceY(g-1,g0) = 12.7
    c: DistanceX(g-1,g0) = 4.08
    c: Coincident(g0,g1)
    c: Coincident(g1,g2)
    c: Coincident(g2,g3)
    c: Coincident(g0,g3)
    c: Horizontal(g3)
    c: Horizontal(g1)
    c: Vertical(g2)
    c: Distance(g1) = 0.905
FEATURE [PartDesign::Pocket] Pocket005
  AllowMultiFace = false
  BaseFeature = -> Pocket004
  Direction = (1,1,1)
  Length = 12.7
  Length2 = 99.9998
  Profile = -> Sketch022
  Type = 0
FEATURE [PartDesign::Chamfer] Chamfer
  Angle = 45
  Base = -> Pocket005 [Edge14]
  BaseFeature = -> Pocket005
  ChamferType = 0
  FlipDirection = false
  Size = 1.8034
  Size2 = 1
  SupportTransform = false
  UseAllEdges = false
FEATURE [Sketcher::SketchObject] Sketch023  label="Mounting hole"
  FullyConstrained = false
  MapMode = 5
  Placement = pos=(0,3.175,0) rot=(0,0.707107,0.707107;3.14159rad)
  Support = -> [Chamfer]
  expr: Constraints[2] = 0.25 in / 2 + 0.003 in
  sketch-geometry (1):
    g0: Circle CenterX=12.7 CenterY=12.7 CenterZ=0 NormalX=0 NormalY=0 NormalZ=1 AngleXU=0 Radius=3.2512
  constraints (3):
    c: DistanceX(g-1,g0) = 12.7
    c: DistanceY(g-1,g0) = 12.7
    c: Radius(g0) = 3.2512
FEATURE [PartDesign::Pocket] Pocket006
  AllowMultiFace = false
  BaseFeature = -> Chamfer
  Direction = (1,1,1)
  Length = 5.00126
  Length2 = 99.9998
  Profile = -> Sketch023
  Type = 1
FEATURE [Sketcher::SketchObject] Sketch024  label="Orienting lip"
  FullyConstrained = false
  MapMode = 5
  Placement = pos=(0,3.175,0) rot=(0,0.707107,0.707107;3.14159rad)
  Support = -> [Pocket006]
  sketch-geometry (6):
    g0: LineSegment StartX=0 StartY=0 StartZ=0 EndX=-3.175 EndY=0 EndZ=0
    g1: LineSegment StartX=-3.175 StartY=0 StartZ=0 EndX=-3.175 EndY=28.575 EndZ=0
    g2: LineSegment StartX=-3.175 StartY=28.575 StartZ=0 EndX=25.4 EndY=28.575 EndZ=0
    g3: LineSegment StartX=25.4 StartY=28.575 StartZ=0 EndX=25.4 EndY=25.4 EndZ=0
    g4: LineSegment StartX=25.4 StartY=25.4 StartZ=0 EndX=0 EndY=25.4 EndZ=0
    g5: LineSegment StartX=0 StartY=25.4 StartZ=0 EndX=0 EndY=0 EndZ=0
  constraints (17):
    c: Coincident(g0,g1)
    c: Coincident(g1,g2)
    c: Coincident(g2,g3)
    c: Coincident(g3,g4)
    c: Coincident(g4,g5)
    c: Coincident(g0,g5)
    c: Coincident(g0,g-1)
    c: Horizontal(g0)
    c: Horizontal(g4)
    c: Horizontal(g2)
    c: Vertical(g1)
    c: Vertical(g5)
    c: Vertical(g3)
    c: DistanceY(g4) = 25.4
    c: DistanceX(g3) = 25.4
    c: DistanceX(g1,g4) = 3.175
    c: DistanceY(g4,g1) = 3.175
FEATURE [PartDesign::Pad] Pad007
  AllowMultiFace = false
  BaseFeature = -> Pocket006
  Direction = (1,1,1)
  Length = 10.795
  Length2 = 99.9998
  Profile = -> Sketch024
  Reversed = true
  Type = 0
FEATURE [PartDesign::Fillet] Fillet
  Base = -> Pad007 [Edge26]
  BaseFeature = -> Pad007
  Radius = 5.08
  SupportTransform = false
  UseAllEdges = false
FEATURE [PartDesign::Body] Body003
  Group = -> [Sketch020,Pad005,Sketch001,Pad006,Sketch021,Sketch022,Sketch023,Pocket004,Pocket005,Chamfer,Pocket006,Sketch024,Pad007,Fillet]
  Origin = -> Origin003
  Placement = pos=(-58.73,-42.01,-2.2e-14) rot=(0.57735,0.57735,0.57735;2.0944rad)
  Tip = -> Fillet
FEATURE [PartDesign::Pad] Pad008
  BaseFeature = -> Pocket003
  Direction = (0,-1,0)
  Length = 67.7
  Length2 = 10
  Placement = pos=(15.25,0,0) rot=(0.57735,0.57735,0.57735;2.0944rad)
  Profile = -> Sketch016
  ReferenceAxis = -> Sketch016 [N_Axis]
  Type = 0
  expr: Length = 55 mm + 0.5 "
FEATURE [Sketcher::SketchObject] Sketch025  label="Rail carrier platform"
  ExternalGeometry = -> [Pad008]
  FullyConstrained = true
  MapMode = 5
  Placement = pos=(15.25,0,1e-16) rot=(0,0,-1;1.5708rad)
  Support = -> [Pad008]
  expr: Constraints[8] = -Spreadsheet.Xmh - 0.5 " - 0.125 "
  expr: Constraints[9] = 1.125 "
  sketch-geometry (4):
    g0: LineSegment StartX=70.5594 StartY=-6.35 StartZ=0 EndX=41.9844 EndY=-6.35 EndZ=0
    g1: LineSegment StartX=41.9844 StartY=-6.35 StartZ=0 EndX=41.9844 EndY=-31.125 EndZ=0
    g2: LineSegment StartX=41.9844 StartY=-31.125 StartZ=0 EndX=70.5594 EndY=-31.125 EndZ=0
    g3: LineSegment StartX=70.5594 StartY=-31.125 StartZ=0 EndX=70.5594 EndY=-6.35 EndZ=0
  constraints (11):
    c: Coincident(g0,g1)
    c: Coincident(g1,g2)
    c: Coincident(g2,g3)
    c: Coincident(g3,g0)
    c: Horizontal(g0)
    c: Horizontal(g2)
    c: Vertical(g1)
    c: Vertical(g3)
    c: DistanceY(g2) = -31.125
    c: DistanceX(g2,g2) = 28.575
    c: Coincident(g0,g-3)
FEATURE [PartDesign::Pad] Pad009
  BaseFeature = -> Pad008
  Direction = (-1e-16,0,1)
  Length = 3.175
  Length2 = 10
  Placement = pos=(15.25,0,0) rot=(0.57735,0.57735,0.57735;2.0944rad)
  Profile = -> Sketch025
  ReferenceAxis = -> Sketch025 [N_Axis]
  Reversed = true
  Type = 0
  expr: Length = 0.125 "
FEATURE [Part::Feature] Part__Feature001  label="Rail-Carrier-0811-E0W"
  Placement = pos=(19.3,-70.6,-18.69) rot=(0.57735,0.57735,0.57735;2.0944rad)
  shape: bbox 39.23 x 25.4 x 16.53 mm, 296 faces, 6 solids (baked)
FEATURE [Part::Feature] Part__Feature002  label="Rail-0783-E0W"
  Placement = pos=(0.45,-70.56,-17.22) rot=(1,0,0;1.5708rad)
  shape: bbox 19.05 x 76.2 x 9.525 mm, 875 faces (baked)
FEATURE [Part::Feature] Part__Feature004  label="Nut-91845A029_18-8 Stainless Steel Hex Nut"
  Placement = pos=(0.44,-57.87,2.82) rot=(0,0,1;0rad)
  shape: bbox 12.83 x 12.83 x 6.51 mm, 39 faces (baked)
FEATURE [Part::Feature] Part__Feature005  label="Post-0336-E0W"
  Placement = pos=(0.39,-57.83,-98.08) rot=(1,0,0;1.5708rad)
  shape: bbox 12.69 x 12.69 x 80.34 mm, 56 faces, 2 solids (baked)
FEATURE [Sketcher::SketchObject] Sketch028  label="ConnectorProfile001"
  FullyConstrained = true
  MapMode = 5
  Placement = pos=(15.25,0,0) rot=(0.57735,0.57735,0.57735;2.0944rad)
  expr: .Placement.Base.x = Spreadsheet.Xmh
  expr: Constraints[23] = -Spreadsheet.Yt
  expr: Constraints[24] = Spreadsheet.ODt
  expr: Constraints[25] = 1.1 * Spreadsheet.ODt
  expr: Constraints[27] = Spreadsheet.Zrt
  expr: Constraints[28] = Spreadsheet.ODt * 2
  sketch-geometry (12):
    g0: ArcOfCircle CenterX=0.315625 CenterY=0 CenterZ=0 NormalX=0 NormalY=0 NormalZ=1 AngleXU=0 Radius=1.74625 StartAngle=3.14159 EndAngle=6.28319
    g1: ArcOfCircle CenterX=0.315625 CenterY=0 CenterZ=0 NormalX=0 NormalY=0 NormalZ=1 AngleXU=0 Radius=3.175 StartAngle=4.71239 EndAngle=6.28319
    g2: ArcOfCircle CenterX=-1.43063 CenterY=4.20125 CenterZ=0 NormalX=0 NormalY=0 NormalZ=1 AngleXU=0 Radius=1.42875 StartAngle=1.5708 EndAngle=3.14159
    g3: ArcOfCircle CenterX=2.06188 CenterY=4.20125 CenterZ=0 NormalX=0 NormalY=0 NormalZ=1 AngleXU=0 Radius=1.42875 StartAngle=0 EndAngle=1.5708
    g4: LineSegment StartX=-2.85937 StartY=4.20125 StartZ=0 EndX=-2.85937 EndY=-3.175 EndZ=0
    g5: LineSegment StartX=-1.43063 StartY=5.63 StartZ=0 EndX=-1.43063 EndY=0 EndZ=0
    g6: LineSegment StartX=2.06188 StartY=5.63 StartZ=0 EndX=2.06188 EndY=0 EndZ=0
    g7: LineSegment StartX=3.49062 StartY=4.20125 StartZ=0 EndX=3.49062 EndY=-9e-16 EndZ=0
    g8: Circle CenterX=0.315625 CenterY=0 CenterZ=0 NormalX=0 NormalY=0 NormalZ=1 AngleXU=0 Radius=1.5875
    g9: GeomPoint X=-1.27188 Y=0 Z=0
    g10: LineSegment StartX=-2.85937 StartY=-3.175 StartZ=0 EndX=0.315625 EndY=-3.175 EndZ=0
    g11: LineSegment StartX=0.315625 StartY=0 StartZ=0 EndX=0.315625 EndY=-3.175 EndZ=0
  constraints (35):
    c: PointOnObject(g0,g-1)
    c: PointOnObject(g0,g-1)
    c: PointOnObject(g0,g-1)
    c: Coincident(g1,g0)
    c: PointOnObject(g1,g-1)
    c: Coincident(g4,g2)
    c: Vertical(g4)
    c: Coincident(g5,g2)
    c: Coincident(g5,g0)
    c: Coincident(g6,g3)
    c: Coincident(g6,g0)
    c: Coincident(g7,g3)
    c: Coincident(g7,g1)
    c: Vertical(g7)
    c: Vertical(g5)
    c: Vertical(g6)
    c: Equal(g3,g2)
    c: PointOnObject(g2,g5)
    c: DistanceY(g2,g2) = 0
    c: DistanceY(g3,g3) = 0
    c: Coincident(g8,g0)
    c: PointOnObject(g9,g8)
    c: PointOnObject(g9,g-1)
    c: DistanceX(g9) = -1.27188
    c: Diameter(g8) = 3.175
    c: Diameter(g0) = 3.4925
    c: DistanceY(g3,g2) = 0
    c: DistanceY(g2) = 5.63
    c: Diameter(g1) = 6.35
    c: Coincident(g10,g4)
    c: Coincident(g10,g1)
    c: Horizontal(g10)
    c: Coincident(g11,g0)
    c: Coincident(g1,g11)
    c: Symmetric(g2,g3,g11)
FEATURE [Sketcher::SketchObject] Sketch029  label="Mounting holes002"
  FullyConstrained = true
  MapMode = 5
  Placement = pos=(0,-1.27187,3e-16) rot=(1,0,0;1.5708rad)
  Support = -> [LinearPattern001]
  expr: Constraints[0] = 0.12 "
  expr: Constraints[15] = Spreadsheet.Xmh
  expr: Constraints[16] = Spreadsheet.DXmh
  expr: Constraints[1] = Spreadsheet.Zrt / 2
  expr: Constraints[5] = 0.219 "
  sketch-geometry (8):
    g0: Circle CenterX=12.075 CenterY=2.815 CenterZ=0 NormalX=0 NormalY=0 NormalZ=1 AngleXU=0 Radius=1.524
    g1: Circle CenterX=18.425 CenterY=2.815 CenterZ=0 NormalX=0 NormalY=0 NormalZ=1 AngleXU=0 Radius=1.524
    g2: Circle CenterX=12.075 CenterY=2.815 CenterZ=0 NormalX=0 NormalY=0 NormalZ=1 AngleXU=0 Radius=2.84073
    g3: Circle CenterX=18.425 CenterY=2.815 CenterZ=0 NormalX=0 NormalY=0 NormalZ=1 AngleXU=0 Radius=2.84073
    g4: GeomPoint X=15.5843 Y=2.815 Z=0
    g5: GeomPoint X=14.9157 Y=2.815 Z=0
    g6: LineSegment StartX=12.075 StartY=2.815 StartZ=0 EndX=18.425 EndY=2.815 EndZ=0
    g7: GeomPoint X=15.25 Y=2.815 Z=0
  constraints (17):
    c: Diameter(g0) = 3.048
    c: DistanceY(g0) = 2.815
    c: Equal(g1,g0)
    c: DistanceY(g0,g1) = 0
    c: Coincident(g2,g0)
    c: Diameter(g2) = 5.68146
    c: Coincident(g3,g1)
    c: Equal(g3,g2)
    c: PointOnObject(g4,g3)
    c: PointOnObject(g5,g2)
    c: Coincident(g6,g0)
    c: Coincident(g6,g1)
    c: PointOnObject(g4,g6)
    c: PointOnObject(g5,g6)
    c: Symmetric(g0,g1,g7)
    c: DistanceX(g7) = 15.25
    c: DistanceX(g0,g1) = 6.35
FEATURE [Sketcher::SketchObject] Sketch030  label="Mounting arm profile001"
  FullyConstrained = true
  MapMode = 5
  Placement = pos=(15.25,-2.85937,2e-16) rot=(0.57735,0.57735,-0.57735;2.0944rad)
  Support = -> [Pocket003]
  expr: Constraints[13] = Spreadsheet.DXmh
  expr: Constraints[14] = -Spreadsheet.Zrt / 2
  expr: Constraints[15] = 0.219 "
  expr: Constraints[16] = Spreadsheet.Wma
  expr: Constraints[18] = Spreadsheet.ODt
  sketch-geometry (8):
    g0: LineSegment StartX=3.175 StartY=6.35 StartZ=0 EndX=0 EndY=6.35 EndZ=0
    g1: LineSegment StartX=0 StartY=6.35 StartZ=0 EndX=0 EndY=-6.35 EndZ=0
    g2: LineSegment StartX=0 StartY=-6.35 StartZ=0 EndX=3.175 EndY=-6.35 EndZ=0
    g3: LineSegment StartX=3.175 StartY=-6.35 StartZ=0 EndX=3.175 EndY=6.35 EndZ=0
    g4: Circle CenterX=-2.815 CenterY=3.175 CenterZ=0 NormalX=0 NormalY=0 NormalZ=1 AngleXU=0 Radius=2.7813
    g5: Circle CenterX=-2.815 CenterY=-3.175 CenterZ=0 NormalX=0 NormalY=0 NormalZ=1 AngleXU=0 Radius=2.7813
    g6: GeomPoint X=-2.815 Y=0.3937 Z=0
    g7: GeomPoint X=-2.815 Y=-0.3937 Z=0
  constraints (20):
    c: Coincident(g0,g1)
    c: Coincident(g1,g2)
    c: Coincident(g2,g3)
    c: Coincident(g3,g0)
    c: Horizontal(g0)
    c: Horizontal(g2)
    c: Vertical(g1)
    c: Equal(g5,g4)
    c: Symmetric(g5,g4,g-1)
    c: PointOnObject(g6,g4)
    c: PointOnObject(g7,g5)
    c: DistanceX(g6,g4) = 0
    c: DistanceX(g7,g5) = 0
    c: DistanceY(g5,g4) = 6.35
    c: DistanceX(g4) = -2.815
    c: Diameter(g4) = 5.5626
    c: DistanceY(g3,g3) = 12.7
    c: Symmetric(g0,g2,g-1)
    c: DistanceX(g0) = 3.175
    c: DistanceX(g0,g0) = 3.175
FEATURE [PartDesign::Pad] Pad011
  Direction = (1,0,0)
  Length = 12.7
  Length2 = 10
  Midplane = true
  Placement = pos=(15.25,0,0) rot=(0.57735,0.57735,0.57735;2.0944rad)
  Profile = -> Sketch028
  ReferenceAxis = -> Sketch028 [N_Axis]
  Type = 0
  expr: Length = Spreadsheet.Wma
FEATURE [PartDesign::Pocket] Pocket008
  BaseFeature = -> Pad011
  Direction = (0,1,-2e-16)
  Length = 5
  Length2 = 5
  Midplane = true
  Placement = pos=(15.25,0,0) rot=(0.57735,0.57735,0.57735;2.0944rad)
  Profile = -> Sketch029
  ReferenceAxis = -> Sketch029 [N_Axis]
  Type = 1
FEATURE [PartDesign::Pad] Pad012
  BaseFeature = -> Pocket008
  Direction = (0,-1,0)
  Length = 12.7
  Length2 = 10
  Placement = pos=(15.25,0,0) rot=(0.57735,0.57735,0.57735;2.0944rad)
  Profile = -> Sketch030
  ReferenceAxis = -> Sketch030 [N_Axis]
  Type = 0
FEATURE [PartDesign::Pad] Pad013
  BaseFeature = -> Pad012
  Direction = (-1,0,0.2)
  Length = 9.99998
  Length2 = 10
  Placement = pos=(15.25,0,0) rot=(0.57735,0.57735,0.57735;2.0944rad)
  Profile = -> Pad012 [Face14]
  Type = 0
  UseCustomVector = true
FEATURE [PartDesign::Pad] Pad014
  BaseFeature = -> Pad013
  Direction = (-1,1e-16,0)
  Length = 31.75
  Length2 = 10
  Placement = pos=(15.25,0,0) rot=(0.57735,0.57735,0.57735;2.0944rad)
  Profile = -> Pad013 [Face22]
  Type = 0
FEATURE [Sketcher::SketchObject] Sketch032  label="Rail carrier platform001"
  ExternalGeometry = -> [Pad014]
  FullyConstrained = true
  MapMode = 5
  Placement = pos=(15.25,0,2) rot=(0,0,-1;1.5708rad)
  Support = -> [Pad014]
  sketch-geometry (4):
    g0: LineSegment StartX=31.4344 StartY=-48.1 StartZ=0 EndX=2.85937 EndY=-48.1 EndZ=0
    g1: LineSegment StartX=2.85937 StartY=-48.1 StartZ=0 EndX=2.85937 EndY=-73.5 EndZ=0
    g2: LineSegment StartX=2.85937 StartY=-73.5 StartZ=0 EndX=31.4344 EndY=-73.5 EndZ=0
    g3: LineSegment StartX=31.4344 StartY=-73.5 StartZ=0 EndX=31.4344 EndY=-48.1 EndZ=0
  constraints (11):
    c: Coincident(g0,g1)
    c: Coincident(g1,g2)
    c: Coincident(g2,g3)
    c: Horizontal(g0)
    c: Horizontal(g2)
    c: Vertical(g1)
    c: Vertical(g3)
    c: DistanceX(g2,g2) = 28.575
    c: DistanceY(g3,g3) = 25.4
    c: Coincident(g0,g3)
    c: Coincident(g-3,g0)
FEATURE [PartDesign::Pad] Pad015
  BaseFeature = -> Pad014
  Direction = (-1e-16,0,1)
  Length = 3.175
  Length2 = 10
  Placement = pos=(15.25,0,0) rot=(0.57735,0.57735,0.57735;2.0944rad)
  Profile = -> Sketch032
  ReferenceAxis = -> Sketch032 [N_Axis]
  Reversed = true
  Type = 0
FEATURE [Sketcher::SketchObject] Sketch026  label="Railer Carrier Mounting Hole"
  ExternalGeometry = -> [Sketch025]
  FullyConstrained = true
  MapMode = 5
  Placement = pos=(15.25,1e-16,2) rot=(0,0,-1;1.5708rad)
  Support = -> [Pad015]
  expr: Constraints[11] = -Spreadsheet.Xmh - 0.5 "
  expr: Constraints[24] = 0.5 "
  expr: Constraints[8] = 1 "
  expr: Constraints[9] = 0.26 "
  sketch-geometry (10):
    g0: LineSegment StartX=45.1594 StartY=-27.95 StartZ=0 EndX=70.5594 EndY=-27.95 EndZ=0
    g1: LineSegment StartX=70.5594 StartY=-27.95 StartZ=0 EndX=70.5594 EndY=-2.55 EndZ=0
    g2: LineSegment StartX=70.5594 StartY=-2.55 StartZ=0 EndX=45.1594 EndY=-2.55 EndZ=0
    g3: LineSegment StartX=45.1594 StartY=-2.55 StartZ=0 EndX=45.1594 EndY=-27.95 EndZ=0
    g4: Circle CenterX=57.8594 CenterY=-15.25 CenterZ=0 NormalX=0 NormalY=0 NormalZ=1 AngleXU=0 Radius=3.302
    g5: ArcOfCircle CenterX=57.8594 CenterY=-8.9 CenterZ=0 NormalX=0 NormalY=0 NormalZ=1 AngleXU=0 Radius=3.302 StartAngle=1e-16 EndAngle=3.14159
    g6: ArcOfCircle CenterX=57.8594 CenterY=-21.6 CenterZ=0 NormalX=0 NormalY=0 NormalZ=1 AngleXU=0 Radius=3.302 StartAngle=3.14159 EndAngle=6.28319
    g7: LineSegment StartX=54.5574 StartY=-8.9 StartZ=0 EndX=54.5574 EndY=-21.6 EndZ=0
    g8: LineSegment StartX=61.1614 StartY=-21.6 StartZ=0 EndX=61.1614 EndY=-8.9 EndZ=0
    g9: LineSegment StartX=57.8594 StartY=-8.9 StartZ=0 EndX=57.8594 EndY=-21.6 EndZ=0
  constraints (25):
    c: Coincident(g0,g1)
    c: Coincident(g1,g2)
    c: Coincident(g2,g3)
    c: Horizontal(g0)
    c: Horizontal(g2)
    c: Vertical(g1)
    c: Vertical(g3)
    c: Equal(g0,g3)
    c: DistanceY(g3,g3) = 25.4
    c: Diameter(g4) = 6.604
    c: Symmetric(g2,g0,g4)
    c: DistanceY(g0) = -27.95
    c: Coincident(g0,g3)
    c: PointOnObject(g0,g-3)
    c: Tangent(g5,g7) = -1.5708
    c: Tangent(g7,g6) = -1.5708
    c: Tangent(g6,g8) = -1.5708
    c: Tangent(g8,g5) = -1.5708
    c: Equal(g5,g6)
    c: Coincident(g9,g5)
    c: Coincident(g9,g6)
    c: Symmetric(g5,g6,g4)
    c: Equal(g4,g6)
    c: Vertical(g9)
    c: DistanceY(g9,g9) = 12.7
FEATURE [PartDesign::Pocket] Pocket007
  BaseFeature = -> Pad009
  Direction = (1e-16,-1e-16,-1)
  Length = 5
  Length2 = 5
  Placement = pos=(15.25,0,0) rot=(0.57735,0.57735,0.57735;2.0944rad)
  Profile = -> Sketch026
  ReferenceAxis = -> Sketch026 [N_Axis]
  Type = 1
FEATURE [Sketcher::SketchObject] Sketch027  label="Rail carrier alignment lip"
  ExternalGeometry = -> [Pocket007]
  FullyConstrained = true
  MapMode = 5
  Placement = pos=(15.25,-2e-16,-3.175) rot=(0.707107,0.707107,0;3.14159rad)
  Support = -> [Pocket007]
  expr: Constraints[7] = 0.125 "
  sketch-geometry (6):
    g0: LineSegment StartX=-2.85937 StartY=6.35 StartZ=0 EndX=-45.1594 EndY=6.35 EndZ=0
    g1: LineSegment StartX=-45.1594 StartY=6.35 StartZ=0 EndX=-45.1594 EndY=-31.125 EndZ=0
    g2: LineSegment StartX=-45.1594 StartY=-31.125 StartZ=0 EndX=-41.9844 EndY=-31.125 EndZ=0
    g3: LineSegment StartX=-41.9844 StartY=-31.125 StartZ=0 EndX=-41.9844 EndY=3.175 EndZ=0
    g4: LineSegment StartX=-41.9844 StartY=3.175 StartZ=0 EndX=-2.85937 EndY=3.175 EndZ=0
    g5: LineSegment StartX=-2.85937 StartY=3.175 StartZ=0 EndX=-2.85937 EndY=6.35 EndZ=0
  constraints (16):
    c: Coincident(g0,g1)
    c: Coincident(g1,g2)
    c: Coincident(g2,g3)
    c: Horizontal(g0)
    c: Horizontal(g2)
    c: Vertical(g1)
    c: Vertical(g3)
    c: DistanceX(g2,g2) = 3.175
    c: Coincident(g2,g-4)
    c: Coincident(g0,g-3)
    c: Coincident(g3,g4)
    c: Horizontal(g4)
    c: Coincident(g4,g5)
    c: Coincident(g5,g0)
    c: Vertical(g5)
    c: Equal(g5,g2)
FEATURE [PartDesign::Pad] Pad010
  BaseFeature = -> Pocket007
  Direction = (1e-16,-1e-16,-1)
  Length = 3.175
  Length2 = 10
  Placement = pos=(15.25,0,0) rot=(0.57735,0.57735,0.57735;2.0944rad)
  Profile = -> Sketch027
  ReferenceAxis = -> Sketch027 [N_Axis]
  Type = 0
  expr: Length = 0.125 "
FEATURE [PartDesign::Chamfer] Chamfer001
  Angle = 45
  Base = -> Pad010 [Edge71,Edge99]
  BaseFeature = -> Pad010
  ChamferType = 0
  FlipDirection = false
  Placement = pos=(15.25,0,0) rot=(0.57735,0.57735,0.57735;2.0944rad)
  Size = 3.1496
  Size2 = 1
  SupportTransform = false
  UseAllEdges = false
  expr: Size = 0.124 "
FEATURE [PartDesign::Body] Body002  label="Mask Mount"
  Group = -> [Sketch014,Pad003,Sketch015,Pocket003,Sketch016,Pad008,Sketch025,Pad009,Sketch026,Pocket007,Sketch027,Pad010,Chamfer001]
  Origin = -> Origin002
  Tip = -> Chamfer001
FEATURE [Sketcher::SketchObject] Sketch033  label="Rail Carrier Mounting Hole001"
  ExternalGeometry = -> [Sketch032]
  FullyConstrained = true
  MapMode = 5
  Placement = pos=(15.25,1e-16,2) rot=(0,0,-1;1.5708rad)
  Support = -> [Pad015]
  expr: Constraints[22] = 0.5 "
  expr: Constraints[8] = 1 "
  expr: Constraints[9] = 0.26 "
  sketch-geometry (10):
    g0: LineSegment StartX=6.03437 StartY=-73.5 StartZ=0 EndX=31.4344 EndY=-73.5 EndZ=0
    g1: LineSegment StartX=31.4344 StartY=-73.5 StartZ=0 EndX=31.4344 EndY=-48.1 EndZ=0
    g2: LineSegment StartX=31.4344 StartY=-48.1 StartZ=0 EndX=6.03437 EndY=-48.1 EndZ=0
    g3: LineSegment StartX=6.03437 StartY=-48.1 StartZ=0 EndX=6.03437 EndY=-73.5 EndZ=0
    g4: Circle CenterX=18.7344 CenterY=-60.8 CenterZ=0 NormalX=0 NormalY=0 NormalZ=1 AngleXU=0 Radius=3.302
    g5: ArcOfCircle CenterX=18.7344 CenterY=-54.45 CenterZ=0 NormalX=0 NormalY=0 NormalZ=1 AngleXU=0 Radius=3.302 StartAngle=0 EndAngle=3.14159
    g6: ArcOfCircle CenterX=18.7344 CenterY=-67.15 CenterZ=0 NormalX=0 NormalY=0 NormalZ=1 AngleXU=0 Radius=3.302 StartAngle=3.14159 EndAngle=6.28319
    g7: LineSegment StartX=15.4324 StartY=-54.45 StartZ=0 EndX=15.4324 EndY=-67.15 EndZ=0
    g8: LineSegment StartX=22.0364 StartY=-67.15 StartZ=0 EndX=22.0364 EndY=-54.45 EndZ=0
    g9: LineSegment StartX=18.7344 StartY=-54.45 StartZ=0 EndX=18.7344 EndY=-67.15 EndZ=0
  constraints (24):
    c: Coincident(g0,g1)
    c: Coincident(g1,g2)
    c: Coincident(g2,g3)
    c: Horizontal(g0)
    c: Horizontal(g2)
    c: Vertical(g1)
    c: Vertical(g3)
    c: Equal(g0,g3)
    c: DistanceY(g3,g3) = 25.4
    c: Diameter(g4) = 6.604
    c: Symmetric(g2,g0,g4)
    c: Coincident(g0,g3)
    c: Tangent(g5,g7) = -1.5708
    c: Tangent(g7,g6) = -1.5708
    c: Tangent(g6,g8) = -1.5708
    c: Tangent(g8,g5) = -1.5708
    c: Equal(g5,g6)
    c: Coincident(g9,g5)
    c: Coincident(g9,g6)
    c: Symmetric(g5,g6,g4)
    c: Equal(g4,g6)
    c: Vertical(g9)
    c: DistanceY(g9,g9) = 12.7
    c: Coincident(g1,g-3)
FEATURE [PartDesign::Pocket] Pocket009
  BaseFeature = -> Pad015
  Direction = (1e-16,-1e-16,-1)
  Length = 5
  Length2 = 5
  Placement = pos=(15.25,0,0) rot=(0.57735,0.57735,0.57735;2.0944rad)
  Profile = -> Sketch033
  ReferenceAxis = -> Sketch033 [N_Axis]
  Type = 1
FEATURE [Sketcher::SketchObject] Sketch034  label="Arm reinforcement lip"
  ExternalGeometry = -> [Pocket009]
  FullyConstrained = true
  MapMode = 5
  Placement = pos=(-58.25,-1.22e-14,-8.2e-15) rot=(0.57735,0.57735,-0.57735;4.18879rad)
  Support = -> [Pocket009]
  sketch-geometry (4):
    g0: LineSegment StartX=-2.85937 StartY=1.175 StartZ=0 EndX=-6.03437 EndY=1.175 EndZ=0
    g1: LineSegment StartX=-6.03437 StartY=1.175 StartZ=0 EndX=-6.03437 EndY=3.175 EndZ=0
    g2: LineSegment StartX=-6.03437 StartY=3.175 StartZ=0 EndX=-2.85937 EndY=3.175 EndZ=0
    g3: LineSegment StartX=-2.85937 StartY=3.175 StartZ=0 EndX=-2.85937 EndY=1.175 EndZ=0
  constraints (11):
    c: Coincident(g0,g1)
    c: Coincident(g1,g2)
    c: Coincident(g2,g3)
    c: Coincident(g3,g0)
    c: Horizontal(g0)
    c: Horizontal(g2)
    c: Vertical(g1)
    c: Vertical(g3)
    c: Coincident(g0,g-3)
    c: PointOnObject(g-4,g2)
    c: DistanceX(g2,g2) = 3.175
FEATURE [PartDesign::Pad] Pad016
  BaseFeature = -> Pocket009
  Direction = (-1,-1e-16,1e-16)
  Length = 10
  Length2 = 10
  Placement = pos=(15.25,0,0) rot=(0.57735,0.57735,0.57735;2.0944rad)
  Profile = -> Sketch034
  ReferenceAxis = -> Sketch034 [N_Axis]
  Reversed = true
  Type = 2
FEATURE [PartDesign::Body] Body004  label="Mask Left Side Mount"
  Group = -> [Sketch028,Sketch029,Sketch030,Pad011,Pocket008,Pad012,Pad013,Pad014,Sketch032,Sketch033,Pad015,Pocket009,Sketch034,Pad016]
  Origin = -> Origin004
  Tip = -> Pad016
FEATURE [Part::Part2DObjectPython] Line  # Draft 2D object (typed FeaturePython)
  Area = 0
  ChamferSize = 0
  Closed = false
  End = (-58.25,-6.03437,2)
  FilletRadius = 0
  Length = 13.0606
  MakeFace = true
  Placement = pos=(-55.202,-18.7344,2) rot=(0,0,1;0rad)
  Points = (2) [(0,0,0),(-3.048,12.7,0)]
  Start = (-55.202,-18.7344,2)
  Subdivisions = 0
FEATURE [Part::Mirroring] Mirror  label="Mask Right Side Mount"
  Base = (0,0,0)
  Normal = (0,-1,0)
  Placement = pos=(30.5054,-3.7e-15,0) rot=(0,0,1;3.14159rad)
  Source = -> Body004
